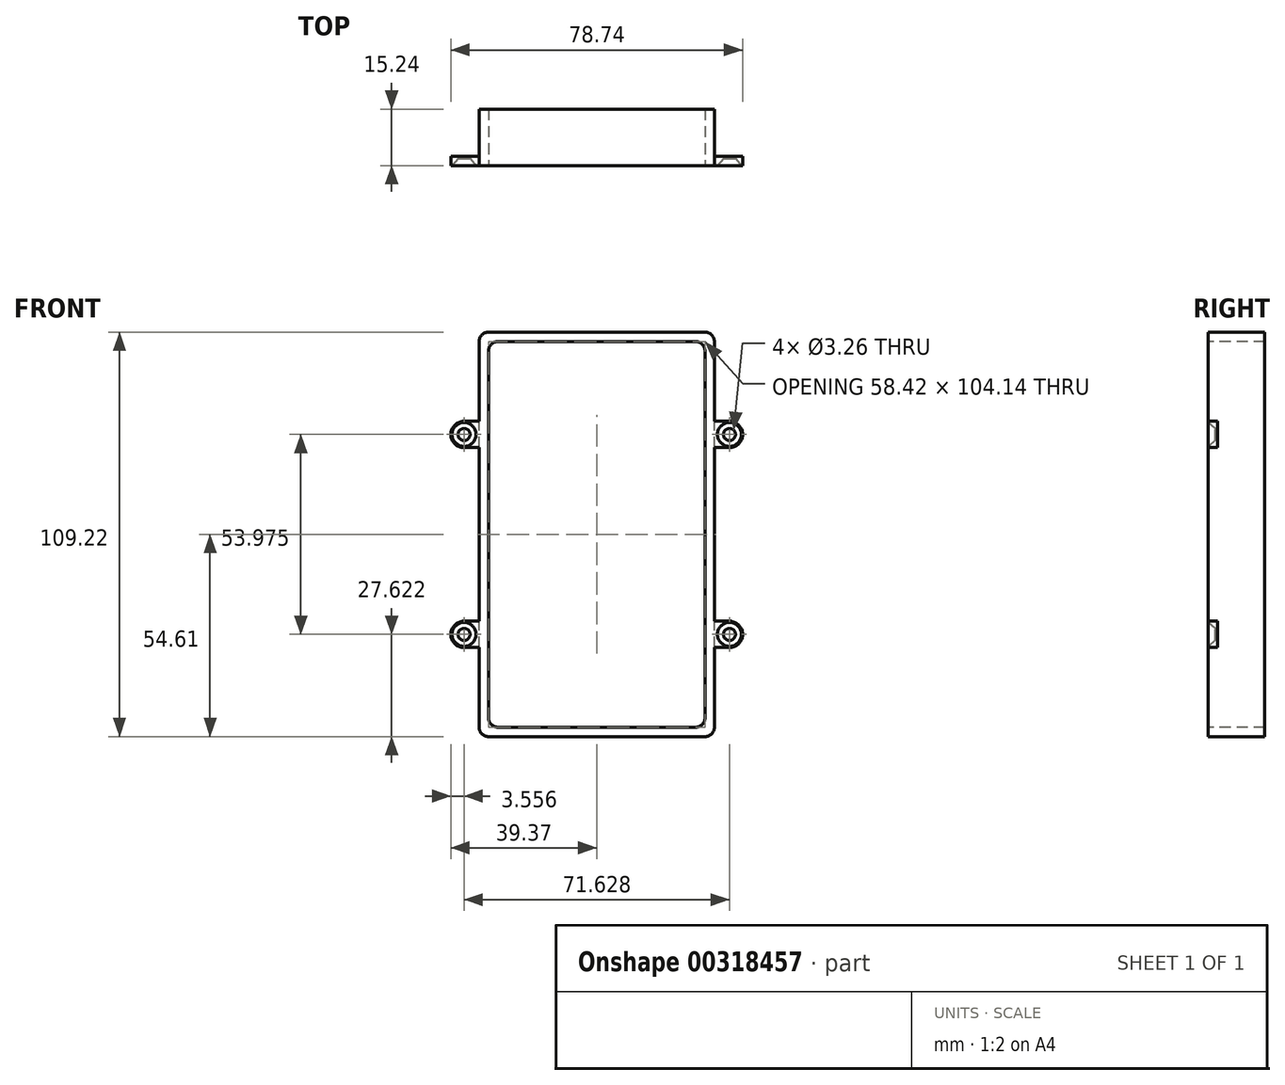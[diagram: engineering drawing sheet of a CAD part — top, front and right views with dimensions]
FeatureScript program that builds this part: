
annotation { "Feature Type Name" : "Feature", "Feature Type Description" : "" }
export const myFeature = defineFeature(function(context is Context, id is Id, definition is map)
    precondition{}
    {
        {
            var Q0;
            Q0=qCreatedBy(makeId("Front.planeOp"),FACE);
            var sketch = newSketch(context, id + "F0", { "sketchPlane" : qUnion([Q0])});
            skLineSegment(sketch, "E0.bottom", {"start": v(-29.21, -54.6) * mm, "end": v(29.21, -54.6) * mm});
            skLineSegment(sketch, "E0.top", {"start": v(-29.21, 54.61) * mm, "end": v(29.2, 54.61) * mm});
            skLineSegment(sketch, "E0.left", {"start": v(-31.75, -52.07) * mm, "end": v(-31.75, 52.07) * mm});
            skLineSegment(sketch, "E0.right", {"start": v(31.75, -52.07) * mm, "end": v(31.75, 52.07) * mm});
            skPoint(sketch, "E0.middle", {"position": v(0, 0) * mm});
            skPoint(sketch, "E1.visualSharp", {"position": v(-31.75, 54.61) * mm});
            skArc(sketch, "E1.filletArc", {"start": v(-29.21, 54.61) * mm, "mid": v(-31, 53.87) * mm, "end": v(-31.75, 52.07) * mm});
            skPoint(sketch, "E2.visualSharp", {"position": v(31.75, 54.61) * mm});
            skArc(sketch, "E2.filletArc", {"start": v(31.75, 52.07) * mm, "mid": v(31, 53.87) * mm, "end": v(29.2, 54.61) * mm});
            skPoint(sketch, "E3.visualSharp", {"position": v(31.75, -54.6) * mm});
            skArc(sketch, "E3.filletArc", {"start": v(29.21, -54.6) * mm, "mid": v(31, -53.87) * mm, "end": v(31.75, -52.07) * mm});
            skPoint(sketch, "E4.visualSharp", {"position": v(-31.75, -54.6) * mm});
            skArc(sketch, "E4.filletArc", {"start": v(-31.75, -52.07) * mm, "mid": v(-31, -53.87) * mm, "end": v(-29.21, -54.6) * mm});
            skSolve(sketch);
        }
        {
            var Q0;
            Q0 = qSketchRegion(id + "F0", true);
            extrude(context, id + "F1", {"entities" : qUnion([Q0]), "depth" : 15.24 * mm, "offsetDistance" : 25.4 * mm});
        }
        {
            var Q0;
            Q0=makeQuery(id+"F1.opExtrude","CAP_FACE",FACE,{"disambiguationData":[OSD([sQuery(id+"F0.wireOp",EDGE,"E0.bottom"),sQuery(id+"F0.wireOp",EDGE,"E0.top"),sQuery(id+"F0.wireOp",EDGE,"E0.left"),sQuery(id+"F0.wireOp",EDGE,"E0.right"),sQuery(id+"F0.wireOp",EDGE,"E1.filletArc"),sQuery(id+"F0.wireOp",EDGE,"E2.filletArc"),sQuery(id+"F0.wireOp",EDGE,"E3.filletArc"),sQuery(id+"F0.wireOp",EDGE,"E4.filletArc")])],"isStart":false});
            var sketch = newSketch(context, id + "F2", { "sketchPlane" : qUnion([Q0])});
            skLineSegment(sketch, "E5.bottom", {"start": v(-31.75, 30.54) * mm, "end": v(-35.81, 30.54) * mm});
            skLineSegment(sketch, "E5.top", {"start": v(-31.75, 23.43) * mm, "end": v(-35.81, 23.43) * mm});
            skLineSegment(sketch, "E5.left", {"start": v(-31.75, 30.54) * mm, "end": v(-31.75, 23.43) * mm});
            skLineSegment(sketch, "E5.right", {"start": v(-39.37, 26.99) * mm, "end": v(-39.37, 26.99) * mm});
            skLineSegment(sketch, "E6.bottom", {"start": v(-31.75, -23.43) * mm, "end": v(-35.81, -23.43) * mm});
            skLineSegment(sketch, "E6.top", {"start": v(-31.75, -30.54) * mm, "end": v(-35.81, -30.54) * mm});
            skLineSegment(sketch, "E6.left", {"start": v(-31.75, -23.43) * mm, "end": v(-31.75, -30.54) * mm});
            skLineSegment(sketch, "E6.right", {"start": v(-39.37, -26.99) * mm, "end": v(-39.37, -26.99) * mm});
            skPoint(sketch, "E7.visualSharp", {"position": v(-39.37, 30.54) * mm});
            skArc(sketch, "E7.filletArc", {"start": v(-35.81, 30.54) * mm, "mid": v(-38.33, 29.5) * mm, "end": v(-39.37, 26.99) * mm});
            skPoint(sketch, "E8.visualSharp", {"position": v(-39.37, 23.43) * mm});
            skArc(sketch, "E8.filletArc", {"start": v(-39.37, 26.99) * mm, "mid": v(-38.33, 24.47) * mm, "end": v(-35.81, 23.43) * mm});
            skPoint(sketch, "E9.visualSharp", {"position": v(-39.37, -23.43) * mm});
            skArc(sketch, "E9.filletArc", {"start": v(-35.81, -23.43) * mm, "mid": v(-38.33, -24.47) * mm, "end": v(-39.37, -26.99) * mm});
            skPoint(sketch, "E10.visualSharp", {"position": v(-39.37, -30.54) * mm});
            skArc(sketch, "E10.filletArc", {"start": v(-39.37, -26.99) * mm, "mid": v(-38.33, -29.5) * mm, "end": v(-35.81, -30.54) * mm});
            skLineSegment(sketch, "E11.MirrorCS", {"start": v(31.75, 30.54) * mm, "end": v(35.81, 30.54) * mm});
            skLineSegment(sketch, "E12.MirrorCS", {"start": v(31.75, 23.43) * mm, "end": v(35.81, 23.43) * mm});
            skLineSegment(sketch, "E13.MirrorCS", {"start": v(31.75, -30.54) * mm, "end": v(35.81, -30.54) * mm});
            skLineSegment(sketch, "E14.MirrorCS", {"start": v(31.75, 30.54) * mm, "end": v(31.75, 23.43) * mm});
            skLineSegment(sketch, "E15.MirrorCS", {"start": v(31.75, -23.43) * mm, "end": v(35.81, -23.43) * mm});
            skLineSegment(sketch, "E16.MirrorCS", {"start": v(31.75, -23.43) * mm, "end": v(31.75, -30.54) * mm});
            skArc(sketch, "E17.MirrorCS", {"start": v(39.37, 26.99) * mm, "mid": v(38.33, 24.47) * mm, "end": v(35.81, 23.43) * mm});
            skArc(sketch, "E18.MirrorCS", {"start": v(35.81, -23.43) * mm, "mid": v(38.33, -24.47) * mm, "end": v(39.37, -26.99) * mm});
            skArc(sketch, "E19.MirrorCS", {"start": v(39.37, -26.99) * mm, "mid": v(38.33, -29.5) * mm, "end": v(35.81, -30.54) * mm});
            skArc(sketch, "E20.MirrorCS", {"start": v(35.81, 30.54) * mm, "mid": v(38.33, 29.5) * mm, "end": v(39.37, 26.99) * mm});
            skPoint(sketch, "E21.MirrorP", {"position": v(39.37, 30.54) * mm});
            skPoint(sketch, "E22.MirrorP", {"position": v(39.37, 23.43) * mm});
            skLineSegment(sketch, "E23.MirrorCS", {"start": v(39.37, 26.99) * mm, "end": v(39.37, 26.99) * mm});
            skPoint(sketch, "E24.MirrorP", {"position": v(39.37, -23.43) * mm});
            skLineSegment(sketch, "E25.MirrorCS", {"start": v(39.37, -26.99) * mm, "end": v(39.37, -26.99) * mm});
            skPoint(sketch, "E26.MirrorP", {"position": v(39.37, -30.54) * mm});
            skSolve(sketch);
        }
        {
            var Q0;
            Q0 = qSketchRegion(id + "F2", true);
            extrude(context, id + "F3", {"entities" : qUnion([Q0]), "operationType" : NewBodyOperationType.ADD, "oppositeDirection" : true, "depth" : 2.54 * mm, "offsetDistance" : 25.4 * mm});
        }
        {
            var Q0;
            Q0=makeQuery(id+"F3.boolean.opBoolean","MERGE",FACE,{"derivedFrom":[makeQuery(id+"F1.opExtrude","CAP_FACE",FACE,{"disambiguationData":[OSD([sQuery(id+"F0.wireOp",EDGE,"E0.bottom"),sQuery(id+"F0.wireOp",EDGE,"E0.top"),sQuery(id+"F0.wireOp",EDGE,"E0.left"),sQuery(id+"F0.wireOp",EDGE,"E0.right"),sQuery(id+"F0.wireOp",EDGE,"E1.filletArc"),sQuery(id+"F0.wireOp",EDGE,"E2.filletArc"),sQuery(id+"F0.wireOp",EDGE,"E3.filletArc"),sQuery(id+"F0.wireOp",EDGE,"E4.filletArc")])],"isStart":false}),makeQuery(id+"F3.opExtrude","CAP_FACE",FACE,{"disambiguationData":[OSD([sQuery(id+"F2.wireOp",EDGE,"E5.bottom"),sQuery(id+"F2.wireOp",EDGE,"E5.top"),sQuery(id+"F2.wireOp",EDGE,"E5.left"),sQuery(id+"F2.wireOp",EDGE,"E7.filletArc"),sQuery(id+"F2.wireOp",EDGE,"E8.filletArc")])],"isStart":true}),makeQuery(id+"F3.opExtrude","CAP_FACE",FACE,{"disambiguationData":[OSD([sQuery(id+"F2.wireOp",EDGE,"E6.bottom"),sQuery(id+"F2.wireOp",EDGE,"E6.top"),sQuery(id+"F2.wireOp",EDGE,"E6.left"),sQuery(id+"F2.wireOp",EDGE,"E9.filletArc"),sQuery(id+"F2.wireOp",EDGE,"E10.filletArc")])],"isStart":true})]});
            var sketch = newSketch(context, id + "F4", { "sketchPlane" : qUnion([Q0])});
            skPoint(sketch, "E27", {"position": v(-35.81, 26.99) * mm});
            skPoint(sketch, "E28", {"position": v(-35.81, -26.99) * mm});
            skPoint(sketch, "E29.MirrorP", {"position": v(35.81, -26.99) * mm});
            skPoint(sketch, "E30.MirrorP", {"position": v(35.81, 26.99) * mm});
            skSolve(sketch);
        }
        {
            var Q0;
            Q0=sQuery(id+"F4.wireOp",VERTEX,"E27");
            var Q1;
            Q1=sQuery(id+"F4.wireOp",VERTEX,"E28");
            var Q2;
            Q2=sQuery(id+"F4.wireOp",VERTEX,"E30.MirrorP");
            var Q3;
            Q3=sQuery(id+"F4.wireOp",VERTEX,"E29.MirrorP");
            var Q4;
            Q4=makeQuery(id+"F1.opExtrude","SWEPT_BODY",BODY,{"disambiguationData":[OSD([sQuery(id+"F0.wireOp",EDGE,"E0.bottom"),sQuery(id+"F0.wireOp",EDGE,"E0.top"),sQuery(id+"F0.wireOp",EDGE,"E0.left"),sQuery(id+"F0.wireOp",EDGE,"E0.right"),sQuery(id+"F0.wireOp",EDGE,"E1.filletArc"),sQuery(id+"F0.wireOp",EDGE,"E2.filletArc"),sQuery(id+"F0.wireOp",EDGE,"E3.filletArc"),sQuery(id+"F0.wireOp",EDGE,"E4.filletArc")])]});
            hole(context, id + "F5", {"style" : HoleStyle.C_SINK, "endStyle" : HoleEndStyle.THROUGH, "standardTappedOrClearance" : lookupTablePath({ "standard" : "ANSI", "fit" : "Normal (ASME)", "size" : "#4", "type" : "Clearance" }), "standardBlindInLast" : lookupTablePath({ "fit" : "Free", "standard" : "ANSI", "size" : "#4", "type" : "Clearance" }), "holeDiameter" : 3.26 * mm, "cSinkDiameter" : 6.48 * mm, "cSinkAngle" : 82 * degree, "majorDiameter" : 6.35 * mm, "isTappedThrough" : true, "tappedDepth" : 3.17 * mm, "tapClearance" : 3, "locations" : qUnion([Q0, Q1, Q2, Q3]), "scope" : qUnion([Q4])});
        }
        {
            var Q0;
            Q0=makeQuery(id+"F3.boolean.opBoolean","MERGE",FACE,{"derivedFrom":[makeQuery(id+"F1.opExtrude","CAP_FACE",FACE,{"disambiguationData":[OSD([sQuery(id+"F0.wireOp",EDGE,"E0.bottom"),sQuery(id+"F0.wireOp",EDGE,"E0.top"),sQuery(id+"F0.wireOp",EDGE,"E0.left"),sQuery(id+"F0.wireOp",EDGE,"E0.right"),sQuery(id+"F0.wireOp",EDGE,"E1.filletArc"),sQuery(id+"F0.wireOp",EDGE,"E2.filletArc"),sQuery(id+"F0.wireOp",EDGE,"E3.filletArc"),sQuery(id+"F0.wireOp",EDGE,"E4.filletArc")])],"isStart":false}),makeQuery(id+"F3.opExtrude","CAP_FACE",FACE,{"disambiguationData":[OSD([sQuery(id+"F2.wireOp",EDGE,"E5.bottom"),sQuery(id+"F2.wireOp",EDGE,"E5.top"),sQuery(id+"F2.wireOp",EDGE,"E5.left"),sQuery(id+"F2.wireOp",EDGE,"E7.filletArc"),sQuery(id+"F2.wireOp",EDGE,"E8.filletArc")])],"isStart":true}),makeQuery(id+"F3.opExtrude","CAP_FACE",FACE,{"disambiguationData":[OSD([sQuery(id+"F2.wireOp",EDGE,"E6.bottom"),sQuery(id+"F2.wireOp",EDGE,"E6.top"),sQuery(id+"F2.wireOp",EDGE,"E6.left"),sQuery(id+"F2.wireOp",EDGE,"E9.filletArc"),sQuery(id+"F2.wireOp",EDGE,"E10.filletArc")])],"isStart":true})]});
            var sketch = newSketch(context, id + "F6", { "sketchPlane" : qUnion([Q0])});
            skLineSegment(sketch, "E31.bottom", {"start": v(26.67, -52.07) * mm, "end": v(-26.67, -52.07) * mm});
            skLineSegment(sketch, "E31.top", {"start": v(26.67, 52.07) * mm, "end": v(-26.67, 52.07) * mm});
            skLineSegment(sketch, "E31.left", {"start": v(29.21, -49.53) * mm, "end": v(29.21, 49.53) * mm});
            skLineSegment(sketch, "E31.right", {"start": v(-29.21, -49.53) * mm, "end": v(-29.21, 49.53) * mm});
            skPoint(sketch, "E31.middle", {"position": v(0, 0) * mm});
            skPoint(sketch, "E32.visualSharp", {"position": v(-29.21, 52.07) * mm});
            skArc(sketch, "E32.filletArc", {"start": v(-26.67, 52.07) * mm, "mid": v(-28.47, 51.33) * mm, "end": v(-29.21, 49.53) * mm});
            skPoint(sketch, "E33.visualSharp", {"position": v(29.21, 52.07) * mm});
            skArc(sketch, "E33.filletArc", {"start": v(29.21, 49.53) * mm, "mid": v(28.47, 51.33) * mm, "end": v(26.67, 52.07) * mm});
            skPoint(sketch, "E34.visualSharp", {"position": v(29.21, -52.07) * mm});
            skArc(sketch, "E34.filletArc", {"start": v(26.67, -52.07) * mm, "mid": v(28.47, -51.33) * mm, "end": v(29.21, -49.53) * mm});
            skPoint(sketch, "E35.visualSharp", {"position": v(-29.21, -52.07) * mm});
            skArc(sketch, "E35.filletArc", {"start": v(-29.21, -49.53) * mm, "mid": v(-28.47, -51.33) * mm, "end": v(-26.67, -52.07) * mm});
            skSolve(sketch);
        }
        {
            var Q0;
            Q0 = qSketchRegion(id + "F6", true);
            extrude(context, id + "F7", {"entities" : qUnion([Q0]), "operationType" : NewBodyOperationType.REMOVE, "endBound" : BoundingType.THROUGH_ALL, "oppositeDirection" : true, "depth" : 25.4 * mm, "offsetDistance" : 25.4 * mm});
        }
    });
